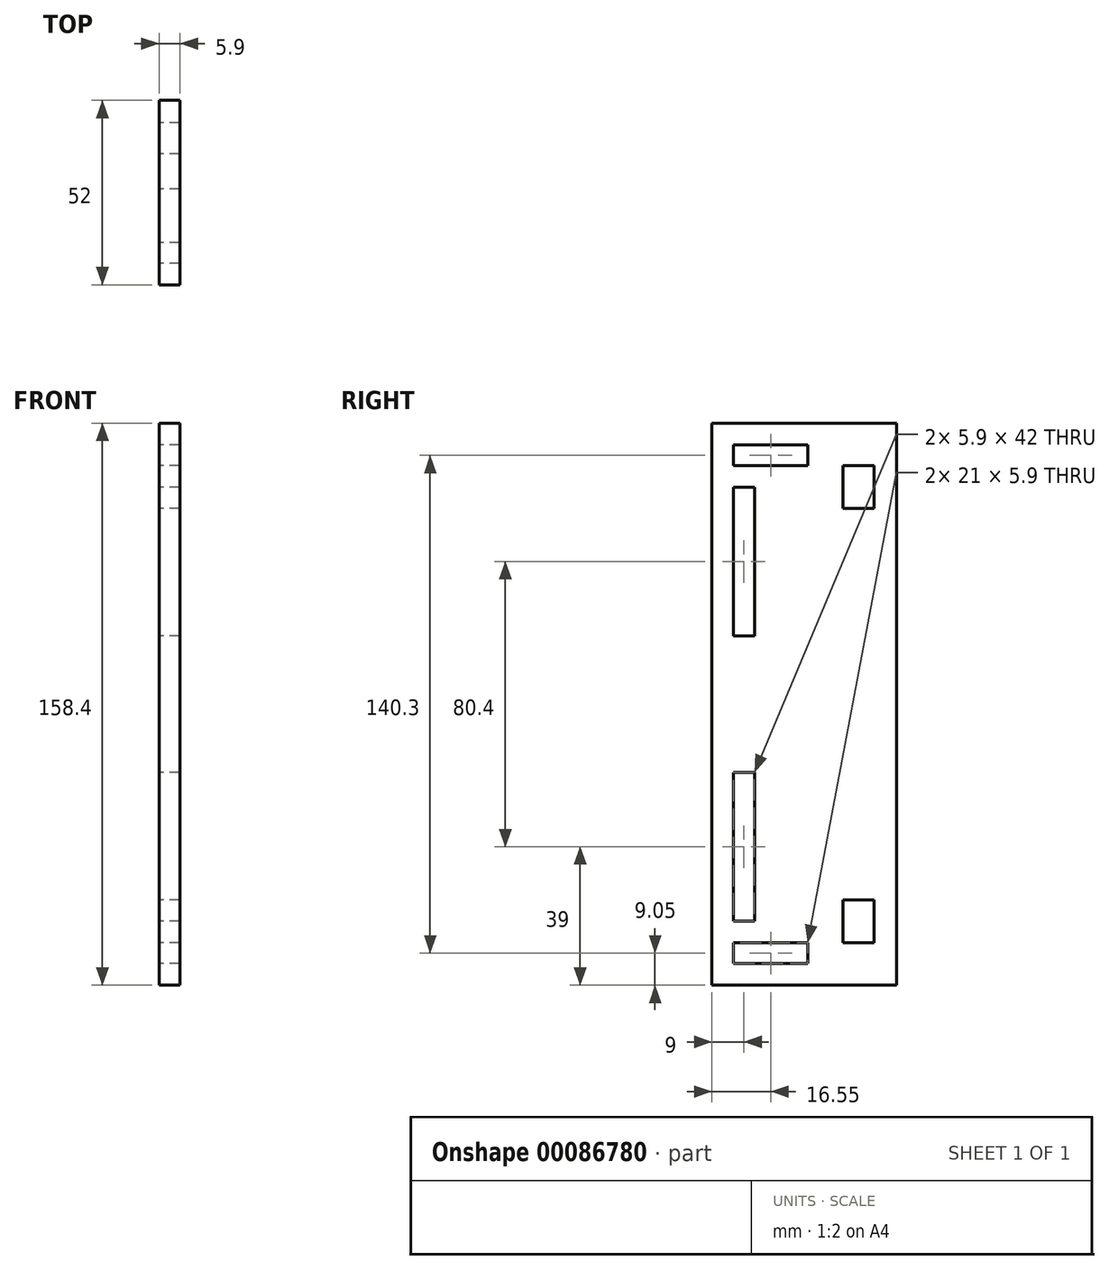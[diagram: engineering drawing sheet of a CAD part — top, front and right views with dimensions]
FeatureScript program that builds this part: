
annotation { "Feature Type Name" : "Feature", "Feature Type Description" : "" }
export const myFeature = defineFeature(function(context is Context, id is Id, definition is map)
    precondition{}
    {
        {
            var Q0;
            Q0=qCreatedBy(makeId("Right.planeOp"),FACE);
            var sketch = newSketch(context, id + "F0", { "sketchPlane" : qUnion([Q0])});
            skLineSegment(sketch, "E0.bottom", {"start": v(26, 79.2) * mm, "end": v(-26, 79.2) * mm});
            skLineSegment(sketch, "E0.top", {"start": v(26, -79.2) * mm, "end": v(-26, -79.2) * mm});
            skLineSegment(sketch, "E0.left", {"start": v(26, 79.2) * mm, "end": v(26, -79.2) * mm});
            skLineSegment(sketch, "E0.right", {"start": v(-26, 79.2) * mm, "end": v(-26, -79.2) * mm});
            skPoint(sketch, "E0.middle", {"position": v(0, 0) * mm});
            skLineSegment(sketch, "E1.bottom", {"start": v(19.7, 67.2) * mm, "end": v(10.95, 67.2) * mm});
            skLineSegment(sketch, "E1.top", {"start": v(19.7, 55.2) * mm, "end": v(10.95, 55.2) * mm});
            skLineSegment(sketch, "E1.left", {"start": v(19.7, 67.2) * mm, "end": v(19.7, 55.2) * mm});
            skLineSegment(sketch, "E1.right", {"start": v(10.95, 67.2) * mm, "end": v(10.95, 55.2) * mm});
            skPoint(sketch, "E1.middle", {"position": v(15.33, 61.2) * mm});
            skLineSegment(sketch, "E2.bottom", {"start": v(1.05, 73.1) * mm, "end": v(-19.95, 73.1) * mm});
            skLineSegment(sketch, "E2.top", {"start": v(1.05, 67.2) * mm, "end": v(-19.95, 67.2) * mm});
            skLineSegment(sketch, "E2.left", {"start": v(1.05, 73.1) * mm, "end": v(1.05, 67.2) * mm});
            skLineSegment(sketch, "E2.right", {"start": v(-19.95, 73.1) * mm, "end": v(-19.95, 67.2) * mm});
            skPoint(sketch, "E2.middle", {"position": v(-9.45, 70.15) * mm});
            skLineSegment(sketch, "E3.bottom", {"start": v(-14.05, 19.2) * mm, "end": v(-19.95, 19.2) * mm});
            skLineSegment(sketch, "E3.top", {"start": v(-14.05, 61.2) * mm, "end": v(-19.95, 61.2) * mm});
            skLineSegment(sketch, "E3.left", {"start": v(-14.05, 19.2) * mm, "end": v(-14.05, 61.2) * mm});
            skLineSegment(sketch, "E3.right", {"start": v(-19.95, 19.2) * mm, "end": v(-19.95, 61.2) * mm});
            skPoint(sketch, "E3.middle", {"position": v(-17, 40.2) * mm});
            skLineSegment(sketch, "E4", {"start": v(-38.29, 67.2) * mm, "end": v(39.9, 67.2) * mm, "construction": true});
            skLineSegment(sketch, "E5.MirrorCS", {"start": v(-14.05, -61.2) * mm, "end": v(-19.95, -61.2) * mm});
            skLineSegment(sketch, "E6.MirrorCS", {"start": v(-19.95, -19.2) * mm, "end": v(-19.95, -61.2) * mm});
            skLineSegment(sketch, "E7.MirrorCS", {"start": v(-14.05, -19.2) * mm, "end": v(-14.05, -61.2) * mm});
            skLineSegment(sketch, "E8.MirrorCS", {"start": v(-14.05, -19.2) * mm, "end": v(-19.95, -19.2) * mm});
            skLineSegment(sketch, "E9.MirrorCS", {"start": v(19.7, -67.2) * mm, "end": v(19.7, -55.2) * mm});
            skLineSegment(sketch, "E10.MirrorCS", {"start": v(19.7, -67.2) * mm, "end": v(10.95, -67.2) * mm});
            skLineSegment(sketch, "E11.MirrorCS", {"start": v(10.95, -67.2) * mm, "end": v(10.95, -55.2) * mm});
            skLineSegment(sketch, "E12.MirrorCS", {"start": v(19.7, -55.2) * mm, "end": v(10.95, -55.2) * mm});
            skLineSegment(sketch, "E13.MirrorCS", {"start": v(-19.95, -73.1) * mm, "end": v(-19.95, -67.2) * mm});
            skLineSegment(sketch, "E14.MirrorCS", {"start": v(1.05, -67.2) * mm, "end": v(-19.95, -67.2) * mm});
            skLineSegment(sketch, "E15.MirrorCS", {"start": v(1.05, -73.1) * mm, "end": v(-19.95, -73.1) * mm});
            skLineSegment(sketch, "E16.MirrorCS", {"start": v(1.05, -73.1) * mm, "end": v(1.05, -67.2) * mm});
            skPoint(sketch, "E17.MirrorP", {"position": v(15.33, -61.2) * mm});
            skPoint(sketch, "E18.MirrorP", {"position": v(-9.45, -70.15) * mm});
            skPoint(sketch, "E19.MirrorP", {"position": v(-17, -40.2) * mm});
            skSolve(sketch);
        }
        {
            var Q0;
            Q0=makeQuery(id+"F0.imprint","IMPRINT",FACE,{"disambiguationData":[TD([[makeQuery(id+"F0.imprint","IMPRINT",EDGE,{"derivedFrom":sQuery(id+"F0.wireOp",EDGE,"E0.bottom")}),1.0]])]});
            extrude(context, id + "F1", {"entities" : qUnion([Q0]), "depth" : 5.9 * mm});
        }
    });
